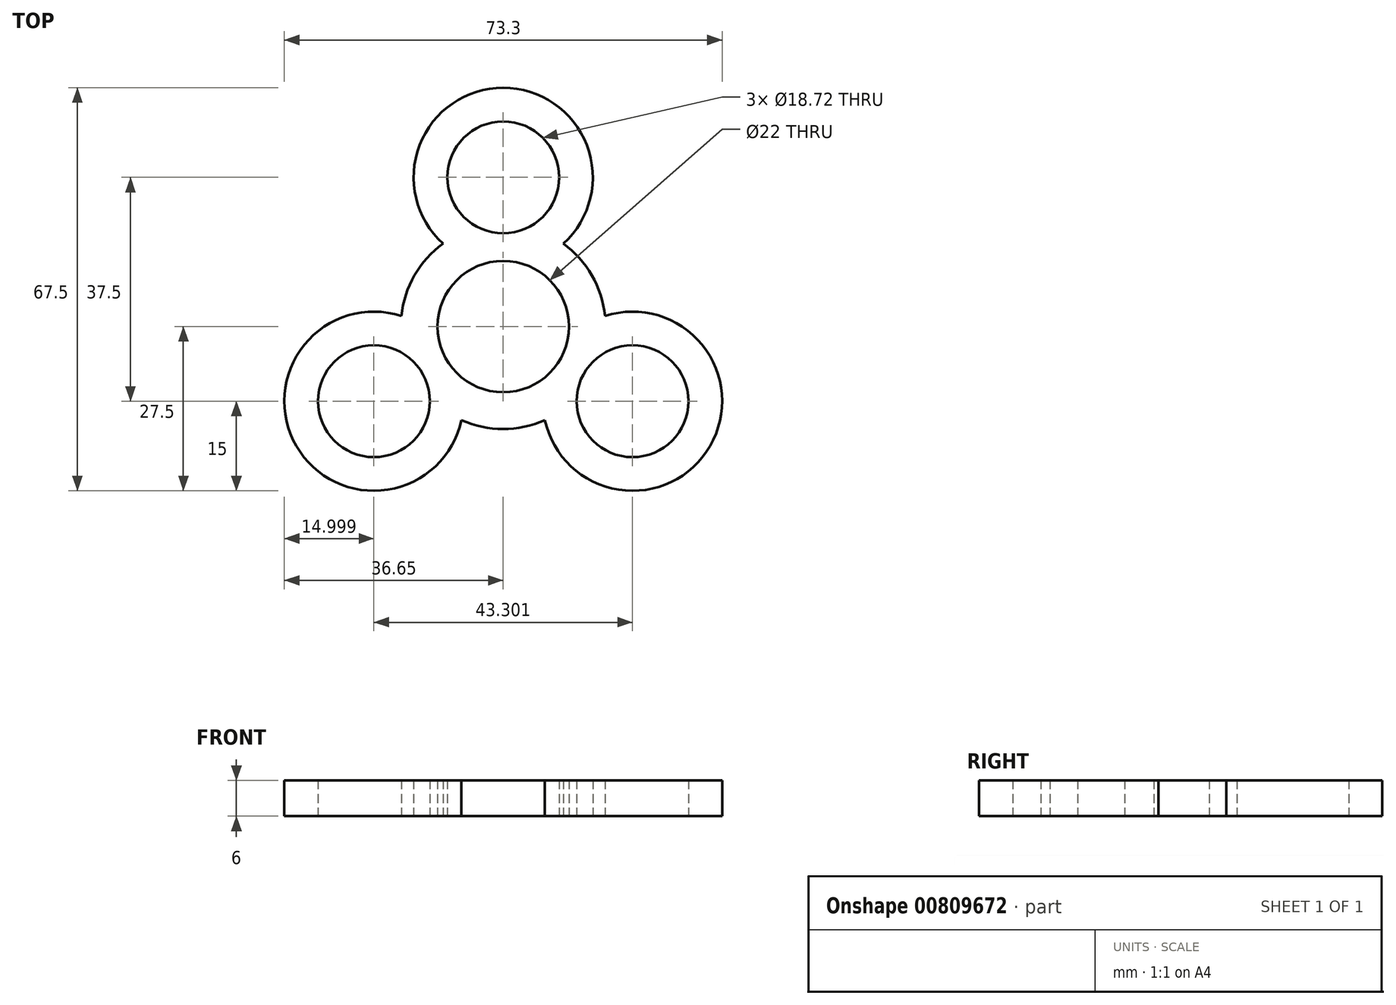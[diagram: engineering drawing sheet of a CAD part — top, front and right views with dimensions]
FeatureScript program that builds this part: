
annotation { "Feature Type Name" : "Feature", "Feature Type Description" : "" }
export const myFeature = defineFeature(function(context is Context, id is Id, definition is map)
    precondition{}
    {
        {
            var Q0;
            Q0=qCreatedBy(makeId("Top.planeOp"),FACE);
            var sketch = newSketch(context, id + "F0", { "sketchPlane" : qUnion([Q0])});
            skArc(sketch, "E0", {"start": v(9.53, 5.5) * mm, "mid": v(0, 11) * mm, "end": v(-9.53, 5.5) * mm});
            skCircle(sketch, "E1", {"center": v(0, 25) * mm, "radius": 9.36 * mm});
            skArc(sketch, "E2", {"start": v(10.07, 13.88) * mm, "mid": v(0, 40) * mm, "end": v(-10.07, 13.88) * mm});
            skArc(sketch, "E3.trimOffspring", {"start": v(-10.07, 13.88) * mm, "mid": v(-12.74, 11.48) * mm, "end": v(-14.85, 8.57) * mm});
            skArc(sketch, "E4.trimOffspring", {"start": v(14.85, 8.57) * mm, "mid": v(12.74, 11.48) * mm, "end": v(10.07, 13.88) * mm});
            skArc(sketch, "E5.1.0", {"start": v(-17.06, 1.78) * mm, "mid": v(-34.64, -20) * mm, "end": v(-6.99, -15.66) * mm});
            skArc(sketch, "E5.2.0", {"start": v(6.99, -15.66) * mm, "mid": v(34.64, -20) * mm, "end": v(17.06, 1.78) * mm});
            skCircle(sketch, "E6.1.0", {"center": v(-21.65, -12.5) * mm, "radius": 9.36 * mm});
            skArc(sketch, "E6.1.1", {"start": v(-9.53, 5.5) * mm, "mid": v(-9.53, -5.5) * mm, "end": v(0, -11) * mm});
            skCircle(sketch, "E6.2.0", {"center": v(21.65, -12.5) * mm, "radius": 9.36 * mm});
            skArc(sketch, "E6.2.1", {"start": v(0, -11) * mm, "mid": v(9.53, -5.5) * mm, "end": v(9.53, 5.5) * mm});
            skArc(sketch, "E7.1.0", {"start": v(-6.99, -15.66) * mm, "mid": v(-3.57, -16.77) * mm, "end": v(0, -17.15) * mm});
            skArc(sketch, "E7.2.0", {"start": v(17.06, 1.78) * mm, "mid": v(16.31, 5.3) * mm, "end": v(14.85, 8.57) * mm});
            skArc(sketch, "E8.1.0", {"start": v(-14.85, 8.57) * mm, "mid": v(-16.31, 5.3) * mm, "end": v(-17.06, 1.78) * mm});
            skArc(sketch, "E8.2.0", {"start": v(0, -17.15) * mm, "mid": v(3.57, -16.77) * mm, "end": v(6.99, -15.66) * mm});
            skSolve(sketch);
        }
        {
            var Q0;
            Q0=makeQuery(id+"F0.imprint","IMPRINT",FACE,{"disambiguationData":[TD([[makeQuery(id+"F0.imprint","IMPRINT",EDGE,{"derivedFrom":sQuery(id+"F0.wireOp",EDGE,"E0")}),-1.0]])]});
            extrude(context, id + "F1", {"entities" : qUnion([Q0]), "depth" : 6 * mm, "offsetDistance" : 25 * mm});
        }
    });
